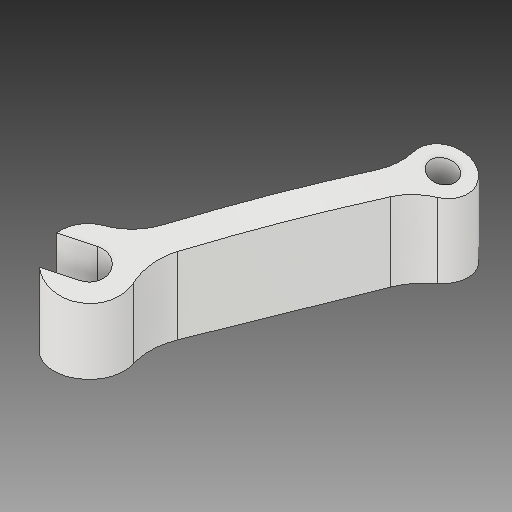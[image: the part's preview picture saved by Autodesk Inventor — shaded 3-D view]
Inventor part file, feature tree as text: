
AUTODESK INVENTOR PART (.ipt)
format: ipt  version: 2017 (Build 210142000, 142)  size: 583,168 bytes
history: native  units: in
note: dims shown in document units (in); Inventor stores cm internally (conversion verified against a paired STEP export)
features: sketch x5, projected_geometry x5, extrude x4, revolve x1, plane x1, pattern_circular x1, fillet x1
ambient origin geometry x8: Origin, YZ Plane, XZ Plane, XY Plane, X Axis, Y Axis, Z Axis, Center Point
bodies: Solid1 (feature_tree)
feature tree (18):
  revolve  "Revolution1"  [1 undecoded]
  plane  "Work Plane1"
  extrude  "Extrusion1"  Depth=0.05in
  pattern_circular  "Circular Pattern1"  [2 undecoded]
  extrude  "Extrusion2"  Depth=0.125in
  extrude  "Extrusion3"  Depth=0.125in
  fillet  "Fillet1"  Radius=0.1in
  extrude  "Extrusion4"  Depth=0.125in TaperAngle=0.0deg
  sketch  "Sketch1"  dims[d0=0.8265in d1=0.175in]
  sketch  "Sketch2"  dims[d2=0.05in d3=0.1in]
  sketch  "Sketch3"  dims[d4=0.15in]
  projected_geometry  "Projected Loop1"
  projected_geometry  "Projected Loop2"
  sketch  "Sketch4"  dims[d5=0.275in]
  projected_geometry  "Projected Loop3"
  projected_geometry  "Projected Loop4"
  sketch  "Sketch5"  dims[d6=90.0deg d7=0.1in d8=0.35in d9=0.2in d10=0.1in d11=1.0in d12=0.0in d13=4.7244in d14=360.0deg d16=0.075in d17=1.0in d18=0.0in d19=0.1in d20=0.025in d22=0.15in d23=0.25in d24=0.14in d25=135.0deg d26=0.05in d27=0.025in d28=0.5in d29=0.2in d30=0.065in d31=1.0in d32=0.0in d33=0.125in d37=0.0197in d38=0.0in]
  projected_geometry  "Projected Loop5"
note: 3 required parameter values undecoded (feature->parameter linkage not recoverable at this tier; creation-order binding heuristic only, values carry confidence <= 0.55)